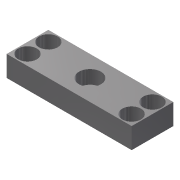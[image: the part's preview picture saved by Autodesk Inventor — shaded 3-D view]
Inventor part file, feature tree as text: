
AUTODESK INVENTOR PART (.ipt)
format: ipt  version: 2015 (Build 190159000, 159)  size: 136,192 bytes
history: native  units: mm
features: hole x5, extrude x1, sketch x1
ambient origin geometry x8: Origin, YZ Plane, XZ Plane, XY Plane, X Axis, Y Axis, Z Axis, Center Point
bodies: Body1 (feature_tree)
feature tree (7):
  extrude  "Extrusion2"  Depth=20.0mm
  hole  "Hole2"  [1 undecoded]
  hole  "Hole3"  [1 undecoded]
  hole  "Hole4"  [1 undecoded]
  hole  "Hole5"  [1 undecoded]
  hole  "Hole6"  [1 undecoded]
  sketch  "Sketch4"  dims[d37=60.0mm d38=20.0mm d39=10.0mm d40=0.0mm d41=10.0mm d42=30.0mm d43=6.5mm d44=6.0mm d45=10.5mm d46=6.5mm d47=90.0deg d48=10.0mm d49=20.594885mm d50=5.0mm d51=5.0mm d52=5.5mm d53=6.0mm d54=9.0mm d55=8.0mm d56=90.0deg d57=10.0mm d58=20.594885mm d59=5.0mm d60=5.0mm d61=5.5mm d62=6.0mm d63=9.0mm d64=8.0mm d65=90.0deg d66=10.0mm d67=20.594885mm d68=5.0mm d69=5.0mm d70=5.5mm d71=6.0mm d72=9.0mm d73=8.0mm d74=90.0deg d75=10.0mm d76=20.594885mm d77=5.0mm d78=5.0mm d79=5.5mm d80=6.0mm d81=9.0mm d82=8.0mm d83=90.0deg d84=10.0mm d85=20.594885mm]
note: 5 required parameter values undecoded (feature->parameter linkage not recoverable at this tier; creation-order binding heuristic only, values carry confidence <= 0.55)
